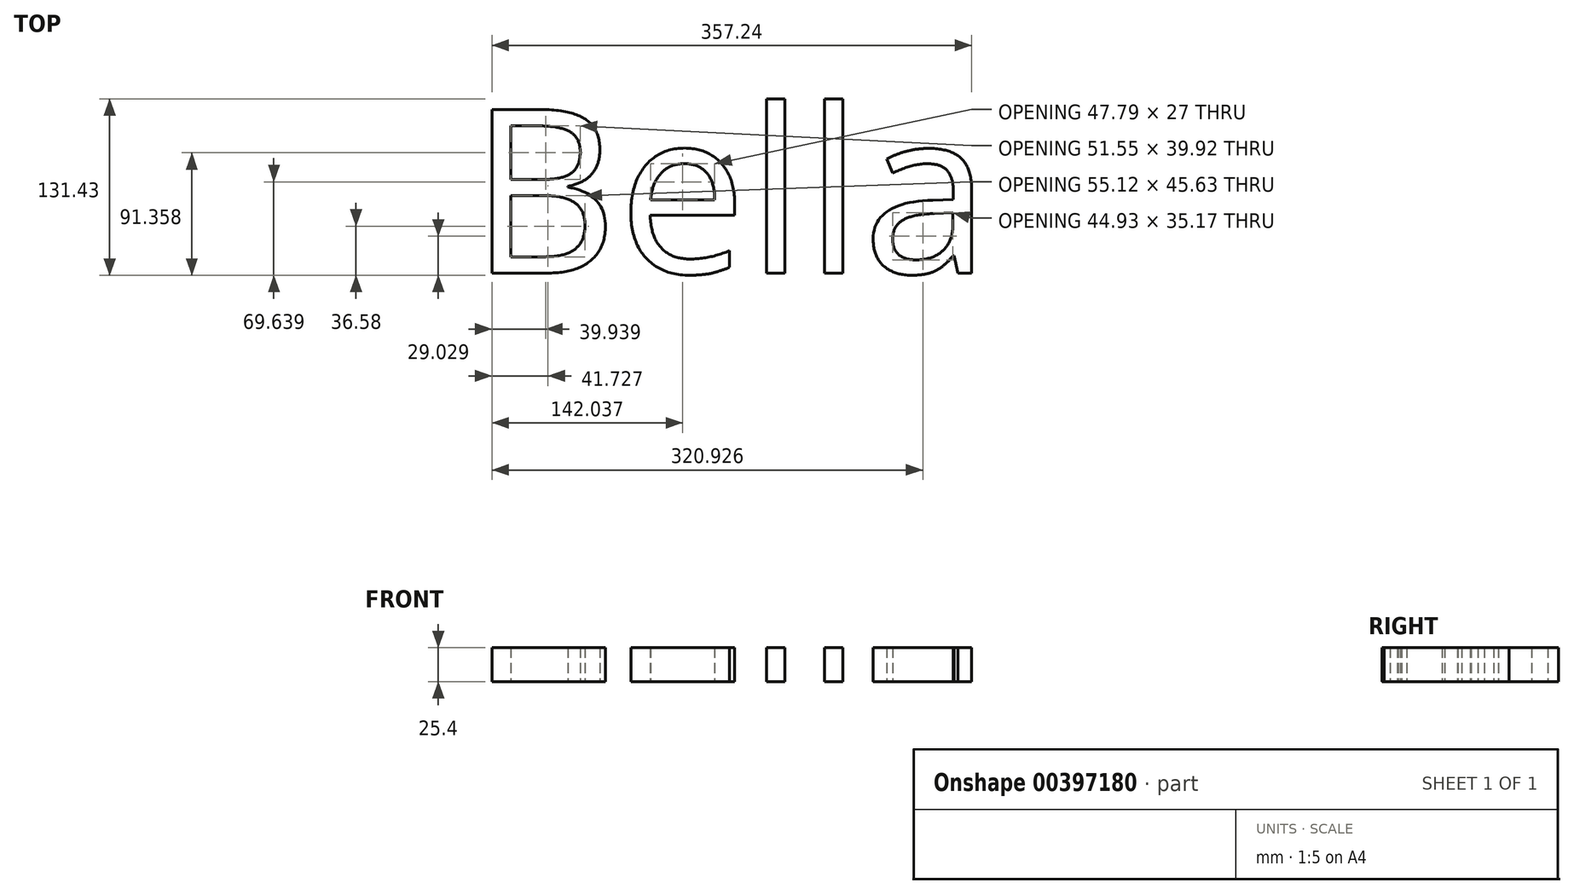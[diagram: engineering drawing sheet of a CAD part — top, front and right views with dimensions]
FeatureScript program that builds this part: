
annotation { "Feature Type Name" : "Feature", "Feature Type Description" : "" }
export const myFeature = defineFeature(function(context is Context, id is Id, definition is map)
    precondition{}
    {
        {
            var Q0;
            Q0=qCreatedBy(makeId("Top.planeOp"),FACE);
            var sketch = newSketch(context, id + "F0", { "sketchPlane" : qUnion([Q0])});
            skText(sketch, "E0", { "text": "Bella\n", "fontName": "OpenSans-Regular.ttf"});
            const initialGuessF0  = {"E0": [-0.14994, -0.05826, 1, 0, 0.12295]};
            skSetInitialGuess(sketch, initialGuessF0);
            skSolve(sketch);
        }
        {
            var Q0;
            Q0 = qSketchRegion(id + "F0", true);
            extrude(context, id + "F1", {"entities" : qUnion([Q0]), "depth" : 25.4 * mm});
        }
    });
